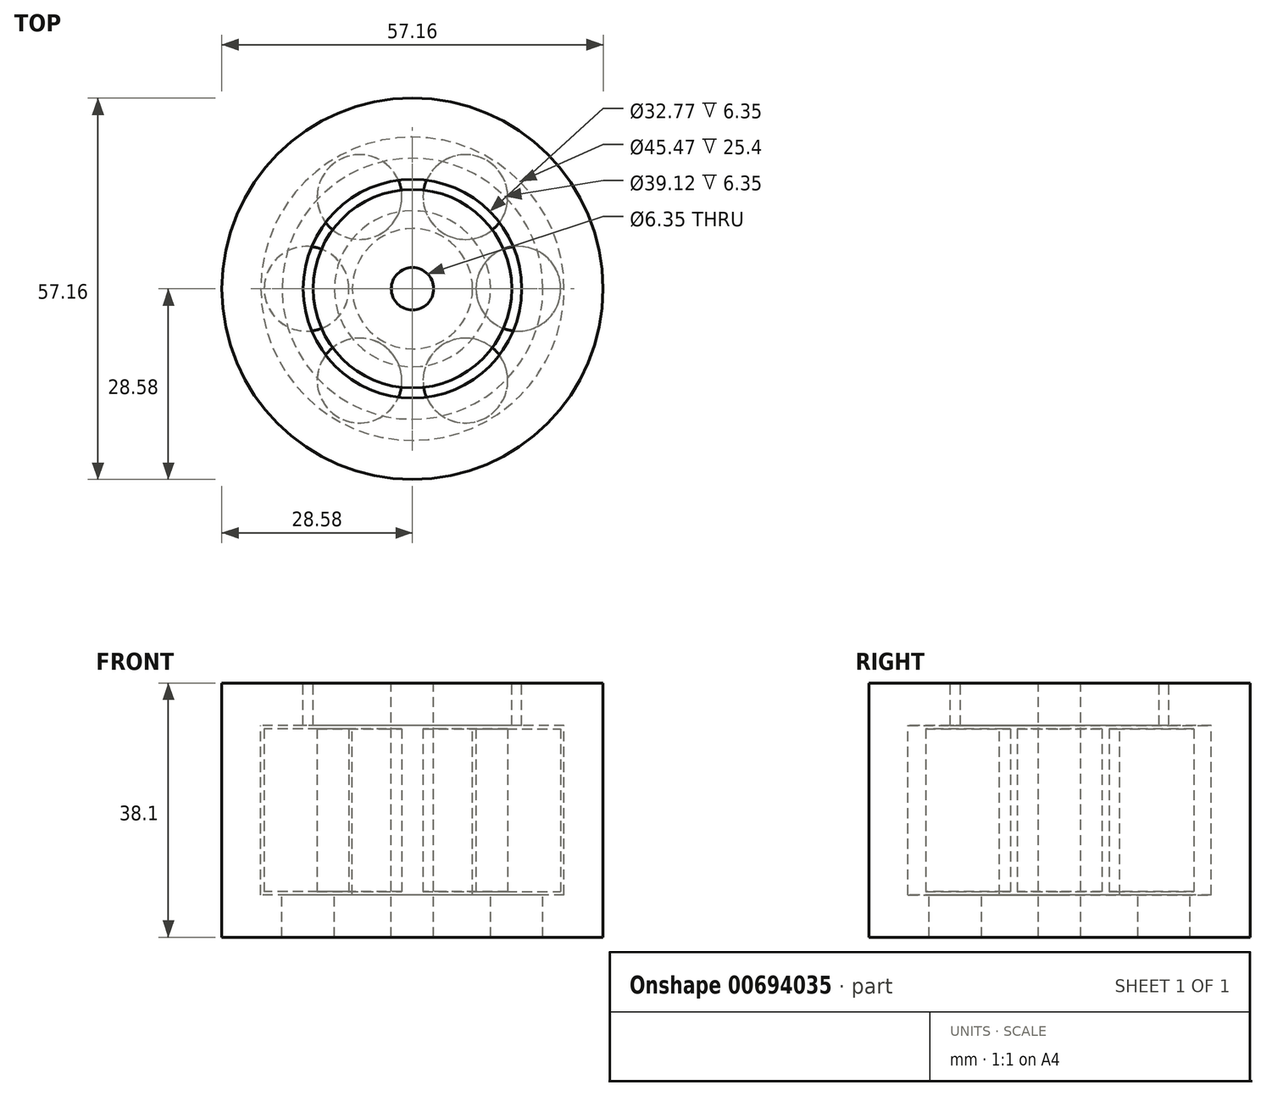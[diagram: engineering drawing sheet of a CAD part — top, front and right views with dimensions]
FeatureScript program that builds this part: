
annotation { "Feature Type Name" : "Feature", "Feature Type Description" : "" }
export const myFeature = defineFeature(function(context is Context, id is Id, definition is map)
    precondition{}
    {
        {
            var Q0;
            Q0=qCreatedBy(makeId("Front.planeOp"),FACE);
            var sketch = newSketch(context, id + "F0", { "sketchPlane" : qUnion([Q0])});
            skLineSegment(sketch, "E0", {"start": v(0, 0) * mm, "end": v(3.18, 0) * mm});
            skLineSegment(sketch, "E1.bottom", {"start": v(3.18, 0) * mm, "end": v(28.58, 0) * mm});
            skLineSegment(sketch, "E1.top", {"start": v(19.56, -38.1) * mm, "end": v(28.58, -38.1) * mm});
            skLineSegment(sketch, "E1.left", {"start": v(3.18, 0) * mm, "end": v(3.18, -38.1) * mm});
            skLineSegment(sketch, "E1.right", {"start": v(28.58, 0) * mm, "end": v(28.58, -38.1) * mm});
            skLineSegment(sketch, "E2", {"start": v(14.88, 0) * mm, "end": v(14.88, -6.35) * mm});
            skLineSegment(sketch, "E3", {"start": v(3.18, 0) * mm, "end": v(3.18, -6.35) * mm});
            skLineSegment(sketch, "E4", {"start": v(9.02, -6.35) * mm, "end": v(14.88, -6.35) * mm});
            skLineSegment(sketch, "E5", {"start": v(3.18, -38.1) * mm, "end": v(3.18, -31.75) * mm});
            skLineSegment(sketch, "E6", {"start": v(9.02, -31.75) * mm, "end": v(11.7, -31.75) * mm});
            skPoint(sketch, "E7.orphan", {"position": v(6.35, -38.1) * mm});
            skPoint(sketch, "E8.orphan", {"position": v(9.53, -38.1) * mm});
            skLineSegment(sketch, "E9", {"start": v(3.18, -38.1) * mm, "end": v(14.88, -38.1) * mm});
            skLineSegment(sketch, "E10", {"start": v(3.18, -38.1) * mm, "end": v(9.02, -38.1) * mm});
            skLineSegment(sketch, "E11", {"start": v(9.02, -31.75) * mm, "end": v(9.02, -6.35) * mm});
            skLineSegment(sketch, "E12", {"start": v(28.58, -38.1) * mm, "end": v(22.73, -38.1) * mm});
            skLineSegment(sketch, "E13", {"start": v(22.73, -31.75) * mm, "end": v(22.73, -6.35) * mm});
            skLineSegment(sketch, "E14.trimOffspring", {"start": v(19.56, -31.75) * mm, "end": v(22.73, -31.75) * mm});
            skPoint(sketch, "E15.start.orphan", {"position": v(15.88, -38.1) * mm});
            skLineSegment(sketch, "E16.trimOffspring", {"start": v(16.38, -6.35) * mm, "end": v(16.38, 0) * mm});
            skLineSegment(sketch, "E17.trimOffspring", {"start": v(16.38, -6.35) * mm, "end": v(22.73, -6.35) * mm});
            skPoint(sketch, "E18.start.orphan", {"position": v(15.88, 0) * mm});
            skLineSegment(sketch, "E19", {"start": v(15.88, 0) * mm, "end": v(15.88, -6.86) * mm});
            skLineSegment(sketch, "E20", {"start": v(15.88, -6.86) * mm, "end": v(22.22, -6.86) * mm});
            skLineSegment(sketch, "E21", {"start": v(22.22, -6.86) * mm, "end": v(9.52, -6.86) * mm});
            skLineSegment(sketch, "E22", {"start": v(9.52, -6.86) * mm, "end": v(9.52, -31.24) * mm});
            skLineSegment(sketch, "E23", {"start": v(9.52, -31.24) * mm, "end": v(22.23, -31.24) * mm});
            skLineSegment(sketch, "E24", {"start": v(22.23, -31.24) * mm, "end": v(22.22, -6.86) * mm});
            skLineSegment(sketch, "E25", {"start": v(15.88, -31.24) * mm, "end": v(15.88, -6.86) * mm});
            skLineSegment(sketch, "E26", {"start": v(0, 0) * mm, "end": v(0, -22.5) * mm});
            skLineSegment(sketch, "E27", {"start": v(19.56, -38.1) * mm, "end": v(19.56, -31.75) * mm});
            skPoint(sketch, "E28.orphan", {"position": v(16.38, -31.75) * mm});
            skLineSegment(sketch, "E29", {"start": v(11.7, -38.1) * mm, "end": v(11.7, -31.75) * mm});
            skSolve(sketch);
        }
        {
            var Q0;
            {var subQ2=sQuery(id+"F0.wireOp",EDGE,"E24");Q0=makeQuery(id+"F0.imprint","IMPRINT",FACE,{"disambiguationData":[TD([[makeQuery(id+"F0.imprint","IMPRINT",EDGE,{"derivedFrom":subQ2}),1.0]])]});}
            var Q1;
            Q1=sQuery(id+"F0.wireOp",EDGE,"E25");
            revolve(context, id + "F1", {"entities" : qUnion([Q0]), "axis" : qUnion([Q1]), "revolveType" : RevolveType.FULL});
        }
        {
            var Q0;
            Q0=qCreatedBy(makeId("Front.planeOp"),FACE);
            var sketch = newSketch(context, id + "F2", { "sketchPlane" : qUnion([Q0])});
            skLineSegment(sketch, "E30", {"start": v(0, 0) * mm, "end": v(0, -36.93) * mm});
            skSolve(sketch);
        }
        {
            var Q0;
            Q0=makeQuery(id+"F1.opRevolve","SWEPT_BODY",BODY,{"disambiguationData":[OSD([sQuery(id+"F0.wireOp",EDGE,"E21"),sQuery(id+"F0.wireOp",EDGE,"E23"),sQuery(id+"F0.wireOp",EDGE,"E24"),sQuery(id+"F0.wireOp",EDGE,"E25")])]});
            var Q1;
            Q1=sQuery(id+"F2.wireOp",EDGE,"E30");
            circularPattern(context, id + "F3", {"entities" : qUnion([Q0]), "axis" : qUnion([Q1]), "angle" : 360 * degree, "instanceCount" : 6, "oppositeDirection" : true, "equalSpace" : true});
        }
        {
            var Q0;
            Q0=makeQuery(id+"F0.imprint","IMPRINT",FACE,{"disambiguationData":[TD([[makeQuery(id+"F0.imprint","IMPRINT",EDGE,{"derivedFrom":sQuery(id+"F0.wireOp",EDGE,"E1.left")}),1.0]])]});
            var Q1;
            Q1=makeQuery(id+"F0.imprint","IMPRINT",FACE,{"disambiguationData":[TD([[makeQuery(id+"F0.imprint","IMPRINT",EDGE,{"derivedFrom":sQuery(id+"F0.wireOp",EDGE,"E1.top")}),1.0]])]});
            var Q2;
            Q2=sQuery(id+"F0.wireOp",EDGE,"E26");
            revolve(context, id + "F4", {"entities" : qUnion([Q0, Q1]), "axis" : qUnion([Q2]), "revolveType" : RevolveType.FULL});
        }
    });
